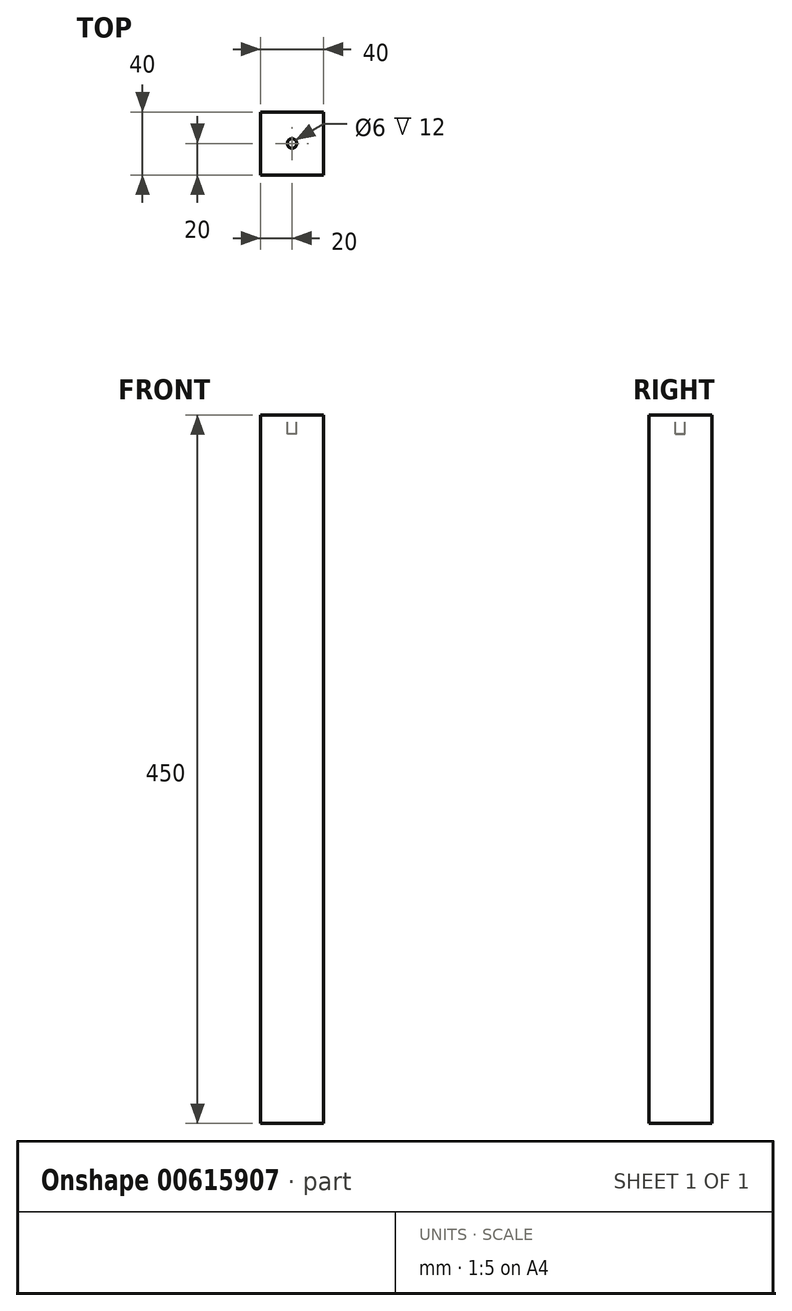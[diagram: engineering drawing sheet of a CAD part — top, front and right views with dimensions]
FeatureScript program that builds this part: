
annotation { "Feature Type Name" : "Feature", "Feature Type Description" : "" }
export const myFeature = defineFeature(function(context is Context, id is Id, definition is map)
    precondition{}
    {
        {
            var Q0;
            Q0=qCreatedBy(makeId("Top.planeOp"),FACE);
            var sketch = newSketch(context, id + "F0", { "sketchPlane" : qUnion([Q0])});
            skLineSegment(sketch, "E0.bottom", {"start": v(0, 0) * mm, "end": v(40, 0) * mm});
            skLineSegment(sketch, "E0.top", {"start": v(0, 40) * mm, "end": v(40, 40) * mm});
            skLineSegment(sketch, "E0.left", {"start": v(0, 0) * mm, "end": v(0, 40) * mm});
            skLineSegment(sketch, "E0.right", {"start": v(40, 0) * mm, "end": v(40, 40) * mm});
            skSolve(sketch);
        }
        {
            var Q0;
            Q0=qSketchRegion(id+"F0",true);
            extrude(context, id + "F1", {"entities" : qUnion([Q0]), "depth" : 450 * mm, "offsetDistance" : 25 * mm});
        }
        {
            var Q0;
            Q0=makeQuery(id+"F1.opExtrude","CAP_FACE",FACE,{"disambiguationData":[OSD([sQuery(id+"F0.wireOp",EDGE,"E0.bottom"),sQuery(id+"F0.wireOp",EDGE,"E0.top"),sQuery(id+"F0.wireOp",EDGE,"E0.left"),sQuery(id+"F0.wireOp",EDGE,"E0.right")])],"isStart":false});
            var sketch = newSketch(context, id + "F2", { "sketchPlane" : qUnion([Q0])});
            skCircle(sketch, "E1", {"center": v(20, 20) * mm, "radius": 3 * mm});
            skPoint(sketch, "E1.centerSnap0", {"position": v(0, 20) * mm});
            skPoint(sketch, "E1.centerSnap1", {"position": v(20, 40) * mm});
            skSolve(sketch);
        }
        {
            var Q0;
            Q0=qSketchRegion(id+"F2",true);
            extrude(context, id + "F3", {"entities" : qUnion([Q0]), "operationType" : NewBodyOperationType.REMOVE, "oppositeDirection" : true, "depth" : 12 * mm, "offsetDistance" : 25 * mm});
        }
    });
